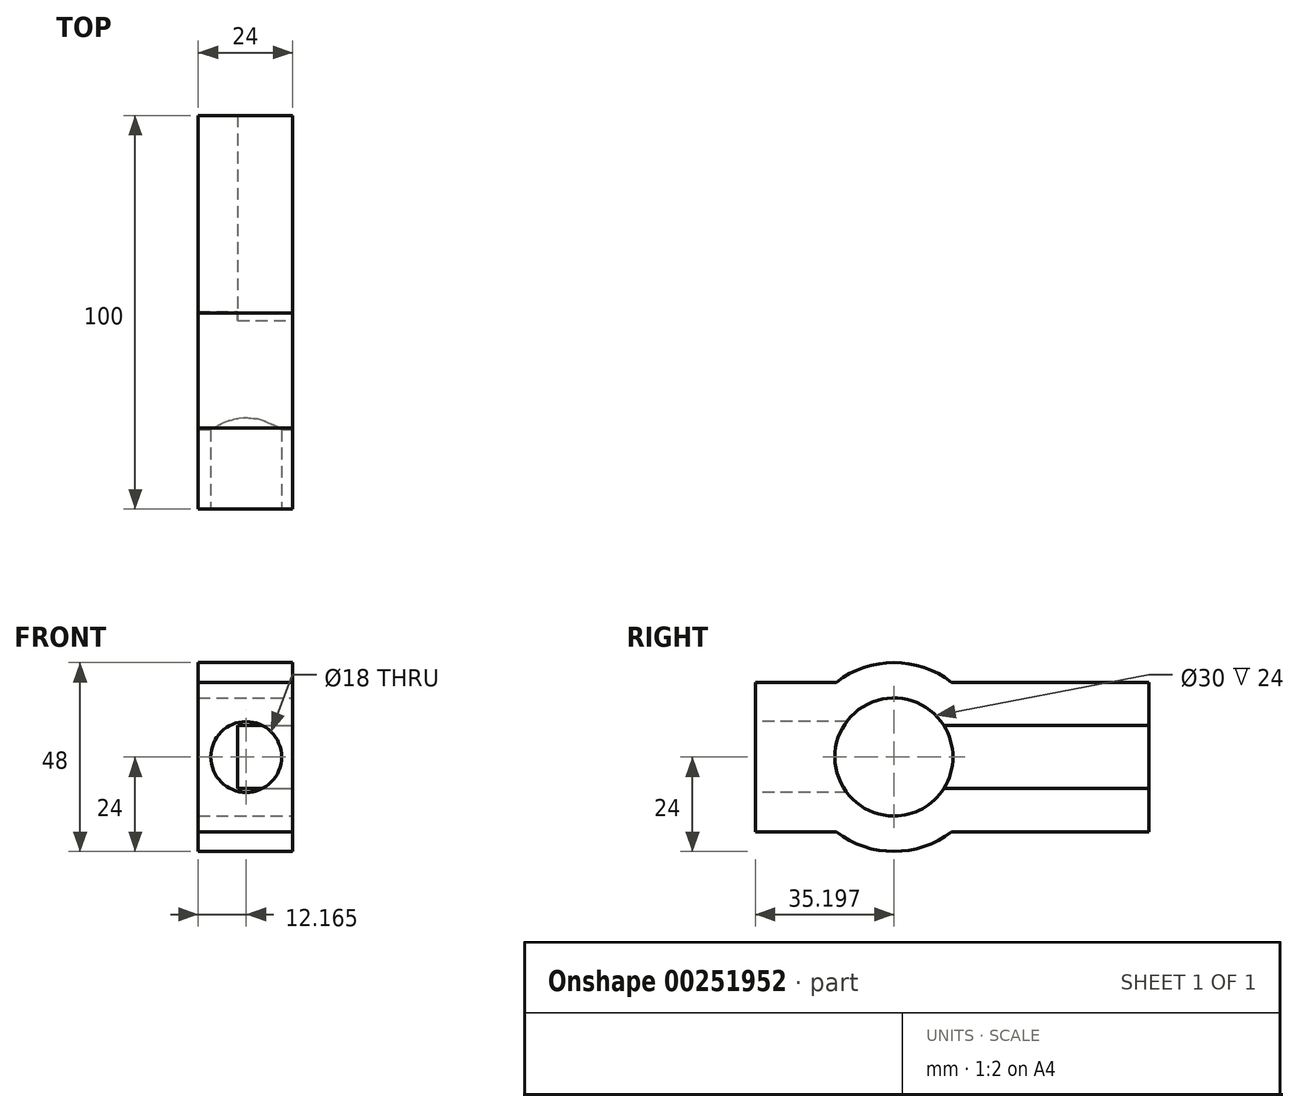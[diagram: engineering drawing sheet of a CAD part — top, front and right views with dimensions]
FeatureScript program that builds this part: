
annotation { "Feature Type Name" : "Feature", "Feature Type Description" : "" }
export const myFeature = defineFeature(function(context is Context, id is Id, definition is map)
    precondition{}
    {
        {
            var Q0;
            Q0=qCreatedBy(makeId("Front.planeOp"),FACE);
            var sketch = newSketch(context, id + "F0", { "sketchPlane" : qUnion([Q0])});
            skLineSegment(sketch, "E0.bottom", {"start": v(12, -19) * mm, "end": v(-12, -19) * mm});
            skLineSegment(sketch, "E0.top", {"start": v(12, 19) * mm, "end": v(-12, 19) * mm});
            skLineSegment(sketch, "E0.left", {"start": v(12, -19) * mm, "end": v(12, 19) * mm});
            skLineSegment(sketch, "E0.right", {"start": v(-12, -19) * mm, "end": v(-12, 19) * mm});
            skPoint(sketch, "E0.middle", {"position": v(0, 0) * mm});
            skSolve(sketch);
        }
        {
            var Q0;
            Q0=makeQuery(id+"F0.imprint","IMPRINT",FACE,{"disambiguationData":[TD([[makeQuery(id+"F0.imprint","IMPRINT",EDGE,{"derivedFrom":sQuery(id+"F0.wireOp",EDGE,"E0.bottom")}),-1.0]])]});
            extrude(context, id + "F1", {"entities" : qUnion([Q0]), "oppositeDirection" : true, "depth" : 100 * mm});
        }
        {
            var Q0;
            Q0=makeQuery(id+"F1.opExtrude","SWEPT_FACE",FACE,{"disambiguationData":[OSD([sQuery(id+"F0.wireOp",EDGE,"E0.left")])]});
            var sketch = newSketch(context, id + "F2", { "sketchPlane" : qUnion([Q0])});
            skLineSegment(sketch, "E1.bottom", {"start": v(0, 19) * mm, "end": v(35, 19) * mm});
            skLineSegment(sketch, "E1.top", {"start": v(0, -19) * mm, "end": v(35, -19) * mm});
            skLineSegment(sketch, "E1.left", {"start": v(0, 19) * mm, "end": v(0, -19) * mm});
            skLineSegment(sketch, "E1.right", {"start": v(35, 19) * mm, "end": v(35, -19) * mm});
            skSolve(sketch);
        }
        {
            var Q0;
            {var subQ0=sQuery(id+"F2.wireOp",EDGE,"E1.right");Q0=makeQuery(id+"F2.imprint","IMPRINT",FACE,{"disambiguationData":[TD([[makeQuery(id+"F2.imprint","IMPRINT",EDGE,{"derivedFrom":subQ0}),1.0]])]});}
            var sketch = newSketch(context, id + "F3", { "sketchPlane" : qUnion([Q0])});
            skCircle(sketch, "E2", {"center": v(35.2, 0) * mm, "radius": 24 * mm});
            skSolve(sketch);
        }
        {
            var Q0;
            Q0 = qSketchRegion(id + "F3", true);
            extrude(context, id + "F4", {"entities" : qUnion([Q0]), "operationType" : NewBodyOperationType.ADD, "oppositeDirection" : true, "depth" : 24 * mm});
        }
        {
            var Q0;
            Q0=makeQuery(id+"F4.boolean.opBoolean","MERGE",FACE,{"derivedFrom":[makeQuery(id+"F1.opExtrude","SWEPT_FACE",FACE,{"disambiguationData":[OSD([sQuery(id+"F0.wireOp",EDGE,"E0.left")])]}),makeQuery(id+"F4.opExtrude","CAP_FACE",FACE,{"disambiguationData":[OSD([sQuery(id+"F3.wireOp",EDGE,"E2")])],"isStart":true})]});
            var sketch = newSketch(context, id + "F5", { "sketchPlane" : qUnion([Q0])});
            skCircle(sketch, "E3", {"center": v(35.2, 0) * mm, "radius": 15 * mm});
            skSolve(sketch);
        }
        {
            var Q0;
            Q0=makeQuery(id+"F5.imprint","IMPRINT",FACE,{"disambiguationData":[TD([[makeQuery(id+"F5.imprint","IMPRINT",EDGE,{"derivedFrom":sQuery(id+"F5.wireOp",EDGE,"E3")}),1.0]])]});
            extrude(context, id + "F6", {"entities" : qUnion([Q0]), "operationType" : NewBodyOperationType.REMOVE, "oppositeDirection" : true, "depth" : 25 * mm});
        }
        {
            var Q0;
            Q0=makeQuery(id+"F4.boolean.opBoolean","MERGE",FACE,{"derivedFrom":[makeQuery(id+"F1.opExtrude","SWEPT_FACE",FACE,{"disambiguationData":[OSD([sQuery(id+"F0.wireOp",EDGE,"E0.left")])]}),makeQuery(id+"F4.opExtrude","CAP_FACE",FACE,{"disambiguationData":[OSD([sQuery(id+"F3.wireOp",EDGE,"E2")])],"isStart":true})]});
            extrude(context, id + "F7", {"entities" : qUnion([Q0]), "operationType" : NewBodyOperationType.ADD, "depth" : 25 * mm});
        }
        {
            var Q0;
            Q0=makeQuery(id+"F7.opExtrude","CAP_FACE",FACE,{"disambiguationData":[OSD([sQuery(id+"F0.wireOp",EDGE,"E0.left"),sQuery(id+"F3.wireOp",EDGE,"E2")])],"isStart":false});
            var sketch = newSketch(context, id + "F8", { "sketchPlane" : qUnion([Q0])});
            skLineSegment(sketch, "E4.bottom", {"start": v(117.8, -8) * mm, "end": v(36.68, -8) * mm});
            skLineSegment(sketch, "E4.top", {"start": v(117.8, 8) * mm, "end": v(36.68, 8) * mm});
            skLineSegment(sketch, "E4.left", {"start": v(117.8, -8) * mm, "end": v(117.8, 8) * mm});
            skLineSegment(sketch, "E4.right", {"start": v(36.68, -8) * mm, "end": v(36.68, 8) * mm});
            skPoint(sketch, "E4.middle", {"position": v(77.24, 0) * mm});
            skSolve(sketch);
        }
        {
            var Q0;
            {var subQ0=sQuery(id+"F8.wireOp",EDGE,"E4.bottom");var subQ4=makeQuery(id+"F7.opExtrude","CAP_EDGE",EDGE,{"disambiguationData":[OSD([sQuery(id+"F5.wireOp",EDGE,"E3")])],"isStart":false});var subQ5=makeQuery(id+"F8.imprint","INTERSECT",VERTEX,{"derivedFrom":[subQ4,subQ0]});Q0=makeQuery(id+"F8.imprint","IMPRINT",FACE,{"disambiguationData":[TD([[makeQuery(id+"F8.imprint","IMPRINT",EDGE,{"disambiguationData":[TD([[subQ5,-1.0]])],"derivedFrom":subQ4}),-1.0]])]});}
            extrude(context, id + "F9", {"entities" : qUnion([Q0]), "operationType" : NewBodyOperationType.REMOVE, "oppositeDirection" : true, "depth" : 14 * mm});
        }
        {
            var Q0;
            Q0=makeQuery(id+"F4.boolean.opBoolean","MERGE",FACE,{"derivedFrom":[makeQuery(id+"F1.opExtrude","SWEPT_FACE",FACE,{"disambiguationData":[OSD([sQuery(id+"F0.wireOp",EDGE,"E0.right")])]}),makeQuery(id+"F4.opExtrude","CAP_FACE",FACE,{"disambiguationData":[OSD([sQuery(id+"F3.wireOp",EDGE,"E2")])],"isStart":false})]});
            extrude(context, id + "F10", {"entities" : qUnion([Q0]), "operationType" : NewBodyOperationType.REMOVE, "oppositeDirection" : true, "depth" : 25 * mm});
        }
        {
            var Q0;
            {var subQ0=sQuery(id+"F0.wireOp",EDGE,"E0.left");Q0=makeQuery(id+"F7.boolean.opBoolean","MERGE",FACE,{"derivedFrom":[makeQuery(id+"F1.opExtrude","CAP_FACE",FACE,{"disambiguationData":[OSD([sQuery(id+"F0.wireOp",EDGE,"E0.bottom"),sQuery(id+"F0.wireOp",EDGE,"E0.top"),subQ0,sQuery(id+"F0.wireOp",EDGE,"E0.right")])],"isStart":true}),makeQuery(id+"F7.opExtrude","SWEPT_FACE",FACE,{"disambiguationData":[OSD([subQ0]),TDD([makeQuery(id+"F1.opExtrude","CAP_EDGE",EDGE,{"disambiguationData":[OSD([subQ0])],"isStart":true})])]})]});}
            var sketch = newSketch(context, id + "F11", { "sketchPlane" : qUnion([Q0])});
            skCircle(sketch, "E5", {"center": v(25.16, 0) * mm, "radius": 9 * mm});
            skSolve(sketch);
        }
        {
            var Q0;
            Q0=makeQuery(id+"F11.imprint","IMPRINT",FACE,{"disambiguationData":[TD([[makeQuery(id+"F11.imprint","IMPRINT",EDGE,{"derivedFrom":sQuery(id+"F11.wireOp",EDGE,"E5")}),1.0]])]});
            extrude(context, id + "F12", {"entities" : qUnion([Q0]), "operationType" : NewBodyOperationType.REMOVE, "oppositeDirection" : true, "depth" : 25 * mm});
        }
    });
